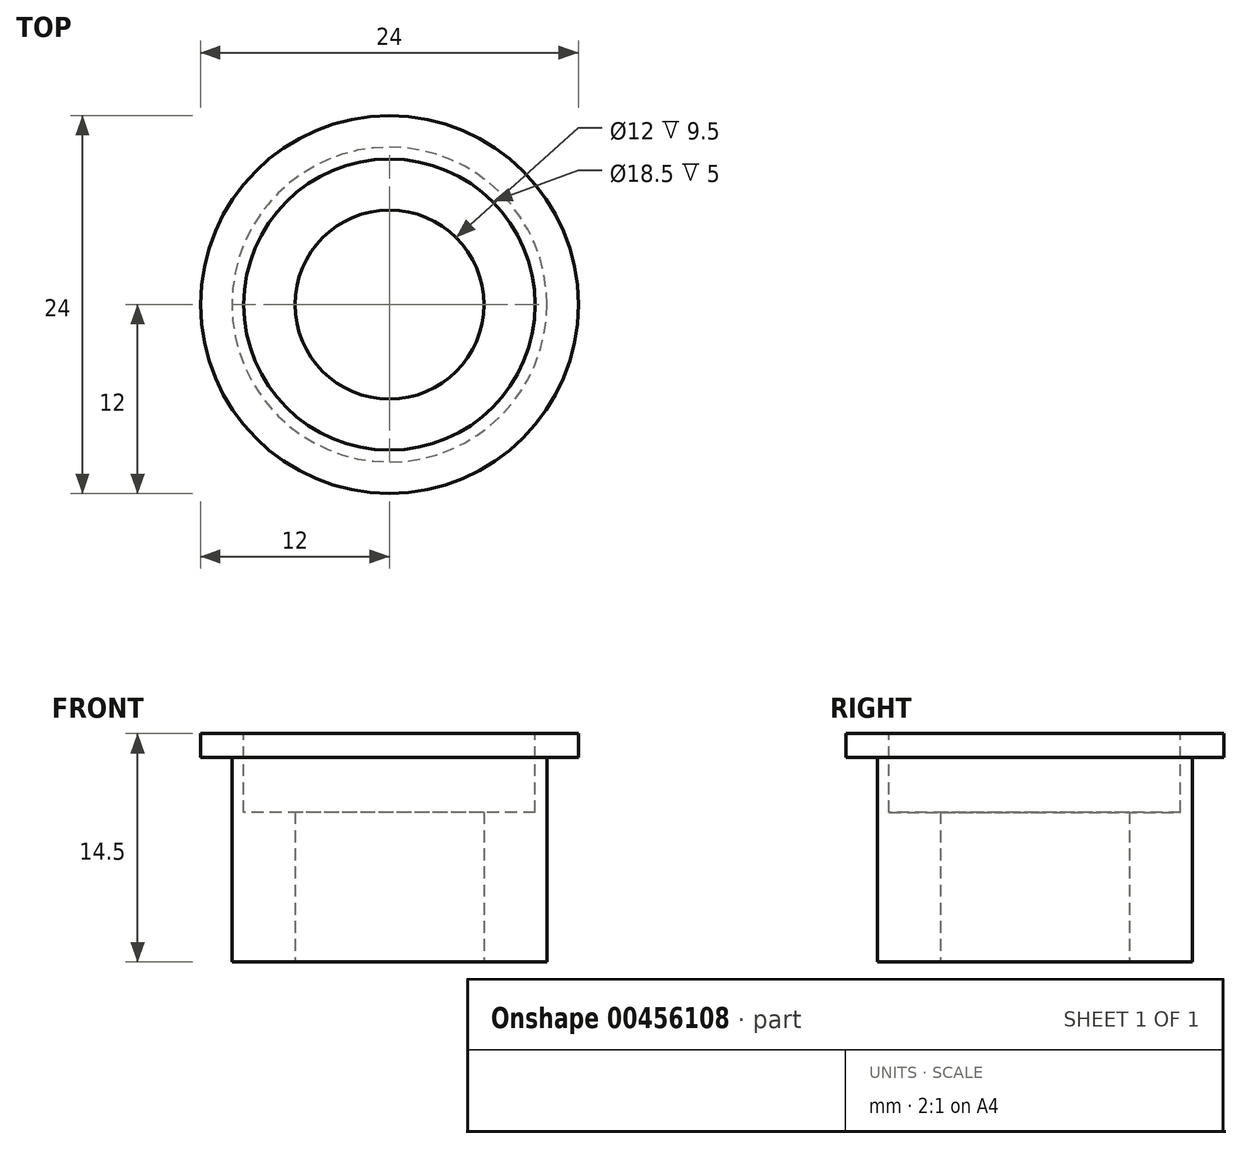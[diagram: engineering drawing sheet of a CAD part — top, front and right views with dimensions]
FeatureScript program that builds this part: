
annotation { "Feature Type Name" : "Feature", "Feature Type Description" : "" }
export const myFeature = defineFeature(function(context is Context, id is Id, definition is map)
    precondition{}
    {
        {
            var Q0;
            Q0=qCreatedBy(makeId("Top.planeOp"),FACE);
            var sketch = newSketch(context, id + "F0", { "sketchPlane" : qUnion([Q0])});
            skCircle(sketch, "E0", {"center": v(0, 0) * mm, "radius": 10 * mm});
            skCircle(sketch, "E1", {"center": v(0, 0) * mm, "radius": 6 * mm});
            skSolve(sketch);
        }
        {
            var Q0;
            Q0=qSketchRegion(id+"F0",true);
            extrude(context, id + "F1", {"entities" : qUnion([Q0]), "depth" : 13 * mm});
        }
        {
            var Q0;
            Q0=makeQuery(id+"F1.opExtrude","CAP_FACE",FACE,{"disambiguationData":[OSD([sQuery(id+"F0.wireOp",EDGE,"E0"),sQuery(id+"F0.wireOp",EDGE,"E1")])],"isStart":false});
            var sketch = newSketch(context, id + "F2", { "sketchPlane" : qUnion([Q0])});
            skCircle(sketch, "E2", {"center": v(0, 0) * mm, "radius": 6 * mm});
            skCircle(sketch, "E3", {"center": v(0, 0) * mm, "radius": 12 * mm});
            skSolve(sketch);
        }
        {
            var Q0;
            Q0=qSketchRegion(id+"F2",true);
            extrude(context, id + "F3", {"entities" : qUnion([Q0]), "operationType" : NewBodyOperationType.ADD, "depth" : 1.5 * mm});
        }
        {
            var Q0;
            Q0=makeQuery(id+"F3.opExtrude","CAP_FACE",FACE,{"disambiguationData":[OSD([sQuery(id+"F2.wireOp",EDGE,"E2"),sQuery(id+"F2.wireOp",EDGE,"E3")])],"isStart":false});
            var sketch = newSketch(context, id + "F4", { "sketchPlane" : qUnion([Q0])});
            skCircle(sketch, "E4", {"center": v(0, 0) * mm, "radius": 6 * mm});
            skCircle(sketch, "E5", {"center": v(0, 0) * mm, "radius": 9.25 * mm});
            skSolve(sketch);
        }
        {
            var Q0;
            Q0 = qSketchRegion(id + "F4", true);
            extrude(context, id + "F5", {"entities" : qUnion([Q0]), "operationType" : NewBodyOperationType.REMOVE, "oppositeDirection" : true, "depth" : 5 * mm});
        }
    });
